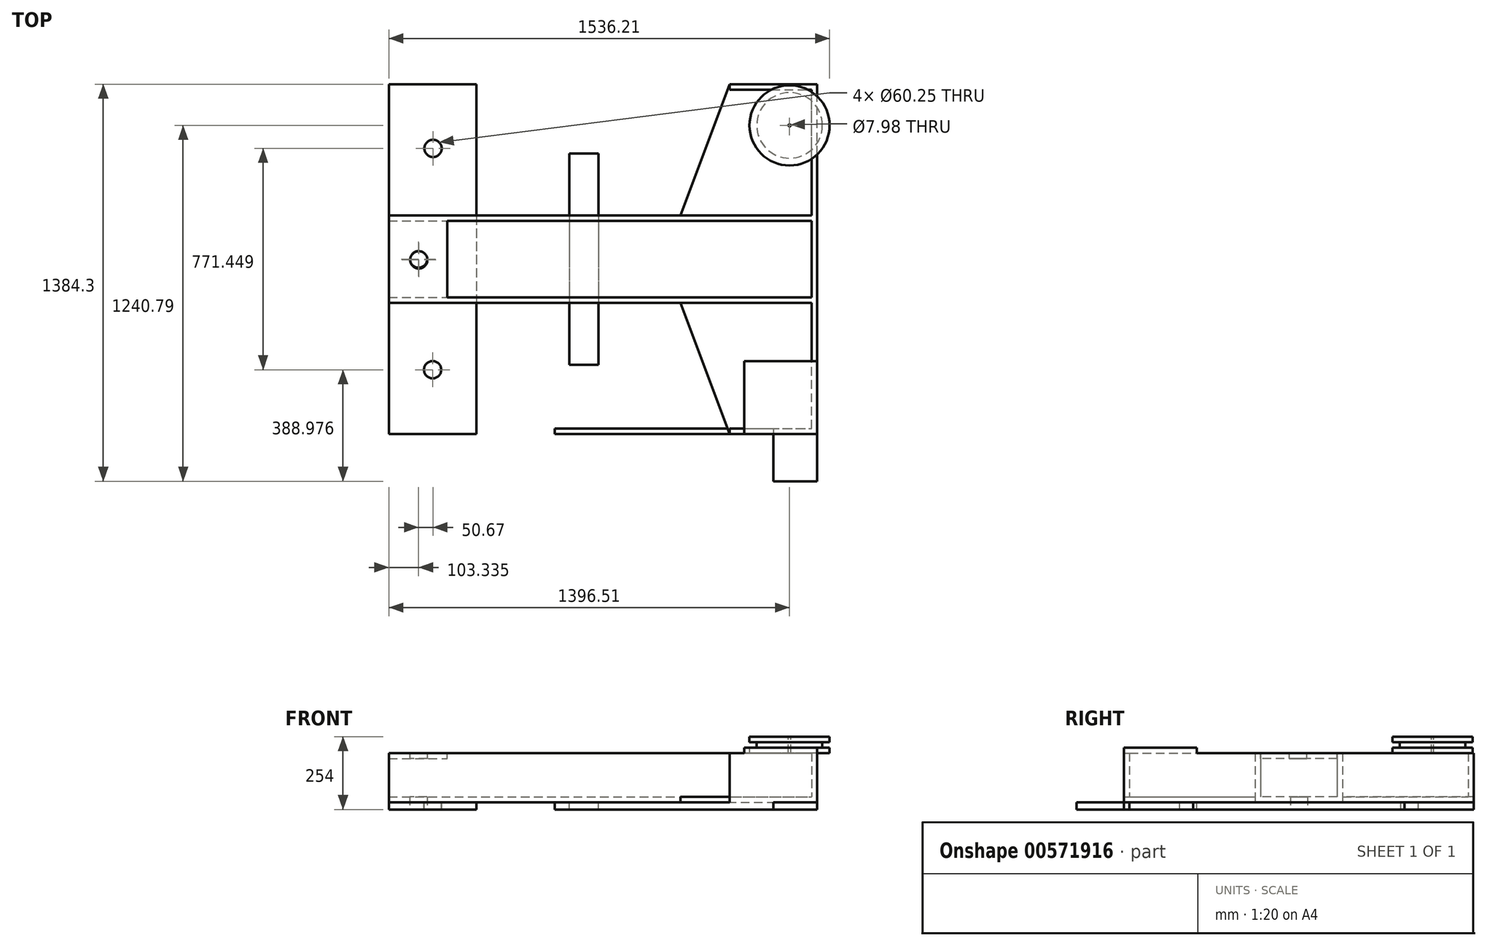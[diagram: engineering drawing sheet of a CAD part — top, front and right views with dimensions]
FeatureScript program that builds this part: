
annotation { "Feature Type Name" : "Feature", "Feature Type Description" : "" }
export const myFeature = defineFeature(function(context is Context, id is Id, definition is map)
    precondition{}
    {
        {
            var Q0;
            Q0=qCreatedBy(makeId("Top.planeOp"),FACE);
            var sketch = newSketch(context, id + "F0", { "sketchPlane" : qUnion([Q0])});
            skLineSegment(sketch, "E0.left", {"start": v(0, 0) * mm, "end": v(0, 1219.2) * mm});
            skLineSegment(sketch, "E1.bottom", {"start": v(-1492.4, 762) * mm, "end": v(-476.4, 762) * mm});
            skLineSegment(sketch, "E1.top", {"start": v(-1492.4, 457.2) * mm, "end": v(-476.4, 457.2) * mm});
            skLineSegment(sketch, "E1.left", {"start": v(-1492.4, 762) * mm, "end": v(-1492.4, 457.2) * mm});
            skLineSegment(sketch, "E1.right", {"start": v(-476.4, 762) * mm, "end": v(-476.4, 457.2) * mm});
            skPoint(sketch, "E2.oppositeSnap0", {"position": v(-1289.2, 914.4) * mm});
            skCircle(sketch, "E3", {"center": v(-1389.08, 609.6) * mm, "radius": 30.12 * mm});
            skPoint(sketch, "E3.centerSnap0", {"position": v(-1492.4, 609.6) * mm});
            skLineSegment(sketch, "E4.bottom", {"start": v(-1492.4, 457.2) * mm, "end": v(0, 457.2) * mm});
            skLineSegment(sketch, "E4.top", {"start": v(-1492.4, 476.25) * mm, "end": v(0, 476.25) * mm});
            skLineSegment(sketch, "E4.left", {"start": v(-1492.4, 457.2) * mm, "end": v(-1492.4, 476.25) * mm});
            skLineSegment(sketch, "E4.right", {"start": v(0, 457.2) * mm, "end": v(0, 476.25) * mm});
            skLineSegment(sketch, "E5.top", {"start": v(-1492.4, 742.95) * mm, "end": v(0, 742.95) * mm});
            skLineSegment(sketch, "E5.left", {"start": v(-1492.4, 762) * mm, "end": v(-1492.4, 742.95) * mm});
            skLineSegment(sketch, "E5.right", {"start": v(0, 762) * mm, "end": v(0, 742.95) * mm});
            skLineSegment(sketch, "E6", {"start": v(0, 0) * mm, "end": v(-304.8, 0) * mm});
            skLineSegment(sketch, "E7", {"start": v(-304.8, 0) * mm, "end": v(-476.4, 457.2) * mm});
            skLineSegment(sketch, "E8", {"start": v(0, 1219.2) * mm, "end": v(-304.8, 1219.2) * mm});
            skLineSegment(sketch, "E9", {"start": v(-304.8, 1219.2) * mm, "end": v(-476.4, 762) * mm});
            skSolve(sketch);
        }
        {
            var Q0;
            Q0 = qSketchRegion(id + "F0", true);
            extrude(context, id + "F1", {"entities" : qUnion([Q0]), "depth" : 19.05 * mm, "offsetDistance" : 25.4 * mm});
        }
        {
            var Q0;
            {var subQ0=sQuery(id+"F0.wireOp",EDGE,"E7");var subQ1=sQuery(id+"F0.wireOp",EDGE,"E6");var subQ2=sQuery(id+"F0.wireOp",EDGE,"E5.bottom");var subQ3=sQuery(id+"F0.wireOp",EDGE,"E8");var subQ4=sQuery(id+"F0.wireOp",EDGE,"E5.right");var subQ5=sQuery(id+"F0.wireOp",EDGE,"E4.right");var subQ6=sQuery(id+"F0.wireOp",EDGE,"E0.left");var subQ7=sQuery(id+"F0.wireOp",EDGE,"E9");var subQ8=sQuery(id+"F0.wireOp",EDGE,"E5.left");var subQ9=sQuery(id+"F0.wireOp",EDGE,"E4.left");var subQ10=sQuery(id+"F0.wireOp",EDGE,"E2.left");var subQ11=sQuery(id+"F0.wireOp",EDGE,"wJzC2NFF-3wZo-U59V-ZQ7f-zWFnnq6j3m8u.left");var subQ12=sQuery(id+"F0.wireOp",EDGE,"E1.left");var subQ13=sQuery(id+"F0.wireOp",EDGE,"E3");var subQ14=sQuery(id+"F0.wireOp",EDGE,"E4.bottom");Q0=makeQuery(id+"FyOnbS3y8ugpvit_1.boolean.opBoolean","SPLIT",FACE,{"disambiguationData":[TD([makeQuery(id+"F1.opExtrude","SWEPT_FACE",FACE,{"disambiguationData":[OSD([subQ13])]})])],"derivedFrom":makeQuery(id+"F1.opExtrude","CAP_FACE",FACE,{"disambiguationData":[OSD([subQ6,subQ12,sQuery(id+"F0.wireOp",EDGE,"wJzC2NFF-3wZo-U59V-ZQ7f-zWFnnq6j3m8u.top"),subQ11,sQuery(id+"F0.wireOp",EDGE,"wJzC2NFF-3wZo-U59V-ZQ7f-zWFnnq6j3m8u.right"),sQuery(id+"F0.wireOp",EDGE,"E2.top"),subQ10,sQuery(id+"F0.wireOp",EDGE,"E2.right"),subQ13,subQ14,subQ9,subQ5,subQ2,subQ8,subQ4,subQ1,subQ0,subQ3,subQ7])],"isStart":false})});}
            var sketch = newSketch(context, id + "F2", { "sketchPlane" : qUnion([Q0])});
            skLineSegment(sketch, "E10", {"start": v(0, 0) * mm, "end": v(-19.05, 0) * mm});
            skLineSegment(sketch, "E11", {"start": v(-19.05, 0) * mm, "end": v(-19.05, 1219.2) * mm});
            skLineSegment(sketch, "E12", {"start": v(-19.05, 1219.2) * mm, "end": v(0, 1219.2) * mm});
            skLineSegment(sketch, "E13", {"start": v(0, 1219.2) * mm, "end": v(0, 0) * mm});
            skSolve(sketch);
        }
        {
            var Q0;
            Q0=makeQuery(id+"F2.imprint","IMPRINT",FACE,{"disambiguationData":[TD([[makeQuery(id+"F2.imprint","IMPRINT",EDGE,{"derivedFrom":sQuery(id+"F2.wireOp",EDGE,"E10")}),-1.0]])]});
            extrude(context, id + "F3", {"entities" : qUnion([Q0]), "operationType" : NewBodyOperationType.ADD, "depth" : 152.4 * mm, "offsetDistance" : 25.4 * mm});
        }
        {
            var Q0;
            {var subQ0=sQuery(id+"F0.wireOp",EDGE,"E7");var subQ1=sQuery(id+"F0.wireOp",EDGE,"E6");var subQ2=sQuery(id+"F0.wireOp",EDGE,"E5.bottom");var subQ3=sQuery(id+"F0.wireOp",EDGE,"E8");var subQ4=sQuery(id+"F0.wireOp",EDGE,"E5.right");var subQ5=sQuery(id+"F0.wireOp",EDGE,"E4.right");var subQ6=sQuery(id+"F0.wireOp",EDGE,"E0.left");var subQ7=sQuery(id+"F0.wireOp",EDGE,"E9");var subQ8=sQuery(id+"F0.wireOp",EDGE,"E5.left");var subQ9=sQuery(id+"F0.wireOp",EDGE,"E4.left");var subQ10=sQuery(id+"F0.wireOp",EDGE,"E2.left");var subQ11=sQuery(id+"F0.wireOp",EDGE,"wJzC2NFF-3wZo-U59V-ZQ7f-zWFnnq6j3m8u.left");var subQ12=sQuery(id+"F0.wireOp",EDGE,"E1.left");var subQ13=sQuery(id+"F0.wireOp",EDGE,"E3");var subQ14=sQuery(id+"F0.wireOp",EDGE,"E4.bottom");Q0=makeQuery(id+"FyOnbS3y8ugpvit_1.boolean.opBoolean","SPLIT",FACE,{"disambiguationData":[TD([makeQuery(id+"F1.opExtrude","SWEPT_FACE",FACE,{"disambiguationData":[OSD([subQ13])]})])],"derivedFrom":makeQuery(id+"F1.opExtrude","CAP_FACE",FACE,{"disambiguationData":[OSD([subQ6,subQ12,sQuery(id+"F0.wireOp",EDGE,"wJzC2NFF-3wZo-U59V-ZQ7f-zWFnnq6j3m8u.top"),subQ11,sQuery(id+"F0.wireOp",EDGE,"wJzC2NFF-3wZo-U59V-ZQ7f-zWFnnq6j3m8u.right"),sQuery(id+"F0.wireOp",EDGE,"E2.top"),subQ10,sQuery(id+"F0.wireOp",EDGE,"E2.right"),subQ13,subQ14,subQ9,subQ5,subQ2,subQ8,subQ4,subQ1,subQ0,subQ3,subQ7])],"isStart":false})});}
            var sketch = newSketch(context, id + "F4", { "sketchPlane" : qUnion([Q0])});
            skLineSegment(sketch, "E14", {"start": v(-19.05, 0) * mm, "end": v(-304.8, 0) * mm});
            skLineSegment(sketch, "E15", {"start": v(-304.8, 0) * mm, "end": v(-304.8, 19.05) * mm});
            skLineSegment(sketch, "E16", {"start": v(-304.8, 19.05) * mm, "end": v(-19.05, 19.05) * mm});
            skLineSegment(sketch, "E17", {"start": v(-19.05, 19.05) * mm, "end": v(-19.05, 0) * mm});
            skLineSegment(sketch, "E18", {"start": v(-19.05, 1219.2) * mm, "end": v(-304.8, 1219.2) * mm});
            skLineSegment(sketch, "E19", {"start": v(-304.8, 1219.2) * mm, "end": v(-304.8, 1200.15) * mm});
            skLineSegment(sketch, "E20", {"start": v(-304.8, 1200.15) * mm, "end": v(-19.05, 1200.15) * mm});
            skLineSegment(sketch, "E21", {"start": v(-19.05, 1200.15) * mm, "end": v(-19.05, 1219.2) * mm});
            skSolve(sketch);
        }
        {
            var Q0;
            Q0=makeQuery(id+"F4.imprint","IMPRINT",FACE,{"disambiguationData":[TD([[makeQuery(id+"F4.imprint","IMPRINT",EDGE,{"derivedFrom":sQuery(id+"F4.wireOp",EDGE,"E14")}),-1.0]])]});
            var Q1;
            Q1=makeQuery(id+"F4.imprint","IMPRINT",FACE,{"disambiguationData":[TD([[makeQuery(id+"F4.imprint","IMPRINT",EDGE,{"derivedFrom":sQuery(id+"F4.wireOp",EDGE,"E18")}),1.0]])]});
            extrude(context, id + "F5", {"entities" : qUnion([Q0, Q1]), "operationType" : NewBodyOperationType.ADD, "depth" : 152.4 * mm, "offsetDistance" : 25.4 * mm});
        }
        {
            var Q0;
            Q0=makeQuery(id+"F1.opExtrude","CAP_FACE",FACE,{"disambiguationData":[OSD([sQuery(id+"F0.wireOp",EDGE,"E0.left"),sQuery(id+"F0.wireOp",EDGE,"E1.bottom"),sQuery(id+"F0.wireOp",EDGE,"E1.left"),sQuery(id+"F0.wireOp",EDGE,"E3"),sQuery(id+"F0.wireOp",EDGE,"E4.bottom"),sQuery(id+"F0.wireOp",EDGE,"E4.left"),sQuery(id+"F0.wireOp",EDGE,"E4.right"),sQuery(id+"F0.wireOp",EDGE,"E5.left"),sQuery(id+"F0.wireOp",EDGE,"E5.right"),sQuery(id+"F0.wireOp",EDGE,"E6"),sQuery(id+"F0.wireOp",EDGE,"E7"),sQuery(id+"F0.wireOp",EDGE,"E8"),sQuery(id+"F0.wireOp",EDGE,"E9")])],"isStart":false});
            var sketch = newSketch(context, id + "F6", { "sketchPlane" : qUnion([Q0])});
            skLineSegment(sketch, "E22.bottom", {"start": v(-1492.4, 762) * mm, "end": v(-19.05, 762) * mm});
            skLineSegment(sketch, "E22.top", {"start": v(-1492.4, 742.95) * mm, "end": v(-19.05, 742.95) * mm});
            skLineSegment(sketch, "E22.left", {"start": v(-1492.4, 762) * mm, "end": v(-1492.4, 742.95) * mm});
            skLineSegment(sketch, "E22.right", {"start": v(-19.05, 762) * mm, "end": v(-19.05, 742.95) * mm});
            skLineSegment(sketch, "E23.bottom", {"start": v(-1492.4, 457.2) * mm, "end": v(-19.05, 457.2) * mm});
            skLineSegment(sketch, "E23.top", {"start": v(-1492.4, 476.25) * mm, "end": v(-19.05, 476.25) * mm});
            skLineSegment(sketch, "E23.left", {"start": v(-1492.4, 457.2) * mm, "end": v(-1492.4, 476.25) * mm});
            skLineSegment(sketch, "E23.right", {"start": v(-19.05, 457.2) * mm, "end": v(-19.05, 476.25) * mm});
            skSolve(sketch);
        }
        {
            var Q0;
            Q0=makeQuery(id+"F6.imprint","IMPRINT",FACE,{"disambiguationData":[TD([[makeQuery(id+"F6.imprint","IMPRINT",EDGE,{"derivedFrom":sQuery(id+"F6.wireOp",EDGE,"E22.top")}),1.0]])]});
            var Q1;
            Q1=makeQuery(id+"F6.imprint","IMPRINT",FACE,{"disambiguationData":[TD([[makeQuery(id+"F6.imprint","IMPRINT",EDGE,{"derivedFrom":sQuery(id+"F6.wireOp",EDGE,"E23.top")}),-1.0]])]});
            extrude(context, id + "F7", {"entities" : qUnion([Q0, Q1]), "operationType" : NewBodyOperationType.ADD, "depth" : 152.4 * mm, "offsetDistance" : 25.4 * mm});
        }
        {
            var Q0;
            Q0=makeQuery(id+"F7.boolean.opBoolean","MERGE",FACE,{"derivedFrom":[makeQuery(id+"F5.boolean.opBoolean","MERGE",FACE,{"derivedFrom":[makeQuery(id+"F3.opExtrude","CAP_FACE",FACE,{"disambiguationData":[OSD([sQuery(id+"F2.wireOp",EDGE,"E10"),sQuery(id+"F2.wireOp",EDGE,"E11"),sQuery(id+"F2.wireOp",EDGE,"E12"),sQuery(id+"F2.wireOp",EDGE,"E13")])],"isStart":false}),makeQuery(id+"F5.opExtrude","CAP_FACE",FACE,{"disambiguationData":[OSD([sQuery(id+"F4.wireOp",EDGE,"E14"),sQuery(id+"F4.wireOp",EDGE,"E15"),sQuery(id+"F4.wireOp",EDGE,"E16"),sQuery(id+"F4.wireOp",EDGE,"E17")])],"isStart":false}),makeQuery(id+"F5.opExtrude","CAP_FACE",FACE,{"disambiguationData":[OSD([sQuery(id+"F4.wireOp",EDGE,"E18"),sQuery(id+"F4.wireOp",EDGE,"E19"),sQuery(id+"F4.wireOp",EDGE,"E20"),sQuery(id+"F4.wireOp",EDGE,"E21")])],"isStart":false})]}),makeQuery(id+"F7.opExtrude","CAP_FACE",FACE,{"disambiguationData":[OSD([sQuery(id+"F6.wireOp",EDGE,"E22.bottom"),sQuery(id+"F6.wireOp",EDGE,"E22.top"),sQuery(id+"F6.wireOp",EDGE,"E22.left"),sQuery(id+"F6.wireOp",EDGE,"E22.right")])],"isStart":false}),makeQuery(id+"F7.opExtrude","CAP_FACE",FACE,{"disambiguationData":[OSD([sQuery(id+"F6.wireOp",EDGE,"E23.bottom"),sQuery(id+"F6.wireOp",EDGE,"E23.top"),sQuery(id+"F6.wireOp",EDGE,"E23.left"),sQuery(id+"F6.wireOp",EDGE,"E23.right")])],"isStart":false})]});
            var sketch = newSketch(context, id + "F8", { "sketchPlane" : qUnion([Q0])});
            skLineSegment(sketch, "E24", {"start": v(-1492.4, 742.95) * mm, "end": v(-1492.4, 476.25) * mm});
            skLineSegment(sketch, "E25", {"start": v(-1492.4, 476.25) * mm, "end": v(-1289.2, 476.25) * mm});
            skLineSegment(sketch, "E26", {"start": v(-1289.2, 476.25) * mm, "end": v(-1289.2, 742.95) * mm});
            skLineSegment(sketch, "E27", {"start": v(-1289.2, 742.95) * mm, "end": v(-1492.4, 742.95) * mm});
            skCircle(sketch, "E28", {"center": v(-1388.19, 606.77) * mm, "radius": 30.12 * mm});
            skLineSegment(sketch, "E29.0.0", {"start": v(-19.05, 457.2) * mm, "end": v(-19.05, 19.05) * mm});
            skLineSegment(sketch, "E29.0.1", {"start": v(-19.05, 19.05) * mm, "end": v(-304.8, 19.05) * mm});
            skLineSegment(sketch, "E29.0.2", {"start": v(-304.8, 19.05) * mm, "end": v(-304.8, 0) * mm});
            skLineSegment(sketch, "E29.0.3", {"start": v(-304.8, 0) * mm, "end": v(0, 0) * mm});
            skLineSegment(sketch, "E29.0.4", {"start": v(0, 0) * mm, "end": v(0, 1219.2) * mm});
            skLineSegment(sketch, "E29.0.5", {"start": v(0, 1219.2) * mm, "end": v(-304.8, 1219.2) * mm});
            skLineSegment(sketch, "E29.0.6", {"start": v(-304.8, 1219.2) * mm, "end": v(-304.8, 1200.15) * mm});
            skLineSegment(sketch, "E29.0.7", {"start": v(-304.8, 1200.15) * mm, "end": v(-19.05, 1200.15) * mm});
            skLineSegment(sketch, "E29.0.8", {"start": v(-19.05, 1200.15) * mm, "end": v(-19.05, 762) * mm});
            skLineSegment(sketch, "E29.0.9", {"start": v(-19.05, 762) * mm, "end": v(-1492.4, 762) * mm});
            skLineSegment(sketch, "E29.0.10", {"start": v(-1492.4, 762) * mm, "end": v(-1492.4, 742.95) * mm});
            skLineSegment(sketch, "E29.0.11", {"start": v(-1492.4, 742.95) * mm, "end": v(-19.05, 742.95) * mm});
            skLineSegment(sketch, "E29.0.12", {"start": v(-19.05, 742.95) * mm, "end": v(-19.05, 476.25) * mm});
            skLineSegment(sketch, "E29.0.13", {"start": v(-19.05, 476.25) * mm, "end": v(-1492.4, 476.25) * mm});
            skLineSegment(sketch, "E29.0.14", {"start": v(-1492.4, 476.25) * mm, "end": v(-1492.4, 457.2) * mm});
            skLineSegment(sketch, "E29.0.15", {"start": v(-1492.4, 457.2) * mm, "end": v(-19.05, 457.2) * mm});
            skSolve(sketch);
        }
        {
            var Q0;
            Q0 = qSketchRegion(id + "F8", true);
            extrude(context, id + "F9", {"entities" : qUnion([Q0]), "operationType" : NewBodyOperationType.ADD, "oppositeDirection" : true, "depth" : 19.05 * mm, "offsetDistance" : 25.4 * mm});
        }
        {
            var Q0;
            Q0=makeQuery(id+"F9.boolean.opBoolean","MERGE",FACE,{"derivedFrom":[makeQuery(id+"F7.boolean.opBoolean","MERGE",FACE,{"derivedFrom":[makeQuery(id+"F5.boolean.opBoolean","MERGE",FACE,{"derivedFrom":[makeQuery(id+"F3.opExtrude","CAP_FACE",FACE,{"disambiguationData":[OSD([sQuery(id+"F2.wireOp",EDGE,"E10"),sQuery(id+"F2.wireOp",EDGE,"E11"),sQuery(id+"F2.wireOp",EDGE,"E12"),sQuery(id+"F2.wireOp",EDGE,"E13")])],"isStart":false}),makeQuery(id+"F5.opExtrude","CAP_FACE",FACE,{"disambiguationData":[OSD([sQuery(id+"F4.wireOp",EDGE,"E14"),sQuery(id+"F4.wireOp",EDGE,"E15"),sQuery(id+"F4.wireOp",EDGE,"E16"),sQuery(id+"F4.wireOp",EDGE,"E17")])],"isStart":false}),makeQuery(id+"F5.opExtrude","CAP_FACE",FACE,{"disambiguationData":[OSD([sQuery(id+"F4.wireOp",EDGE,"E18"),sQuery(id+"F4.wireOp",EDGE,"E19"),sQuery(id+"F4.wireOp",EDGE,"E20"),sQuery(id+"F4.wireOp",EDGE,"E21")])],"isStart":false})]}),makeQuery(id+"F7.opExtrude","CAP_FACE",FACE,{"disambiguationData":[OSD([sQuery(id+"F6.wireOp",EDGE,"E22.bottom"),sQuery(id+"F6.wireOp",EDGE,"E22.top"),sQuery(id+"F6.wireOp",EDGE,"E22.left"),sQuery(id+"F6.wireOp",EDGE,"E22.right")])],"isStart":false}),makeQuery(id+"F7.opExtrude","CAP_FACE",FACE,{"disambiguationData":[OSD([sQuery(id+"F6.wireOp",EDGE,"E23.bottom"),sQuery(id+"F6.wireOp",EDGE,"E23.top"),sQuery(id+"F6.wireOp",EDGE,"E23.left"),sQuery(id+"F6.wireOp",EDGE,"E23.right")])],"isStart":false})]}),makeQuery(id+"F9.opExtrude","CAP_FACE",FACE,{"disambiguationData":[OSD([sQuery(id+"F8.wireOp",EDGE,"E24"),sQuery(id+"F8.wireOp",EDGE,"E25"),sQuery(id+"F8.wireOp",EDGE,"E26"),sQuery(id+"F8.wireOp",EDGE,"E27"),sQuery(id+"F8.wireOp",EDGE,"E28")])],"isStart":true})]});
            var sketch = newSketch(context, id + "F10", { "sketchPlane" : qUnion([Q0])});
            skLineSegment(sketch, "E30", {"start": v(-19.05, 1019.81) * mm, "end": v(-199.4, 1200.15) * mm});
            skLineSegment(sketch, "E31", {"start": v(-199.4, 1200.15) * mm, "end": v(-237.5, 1200.15) * mm});
            skLineSegment(sketch, "E32", {"start": v(-19.05, 1019.81) * mm, "end": v(-19.05, 981.71) * mm});
            skLineSegment(sketch, "E33", {"start": v(-19.05, 981.71) * mm, "end": v(-237.49, 1200.15) * mm});
            skLineSegment(sketch, "E34", {"start": v(-19.05, 19.05) * mm, "end": v(-199.92, 19.05) * mm});
            skSolve(sketch);
        }
        {
            var Q0;
            Q0 = qSketchRegion(id + "F10", true);
            extrude(context, id + "F11", {"entities" : qUnion([Q0]), "oppositeDirection" : true, "depth" : 19.05 * mm, "offsetDistance" : 25.4 * mm});
        }
        {
            var Q0;
            Q0=makeQuery(id+"F11.boolean.opBoolean","MERGE",FACE,{"derivedFrom":[makeQuery(id+"F9.boolean.opBoolean","MERGE",FACE,{"derivedFrom":[makeQuery(id+"F7.boolean.opBoolean","MERGE",FACE,{"derivedFrom":[makeQuery(id+"F5.boolean.opBoolean","MERGE",FACE,{"derivedFrom":[makeQuery(id+"F3.opExtrude","CAP_FACE",FACE,{"disambiguationData":[OSD([sQuery(id+"F2.wireOp",EDGE,"E10"),sQuery(id+"F2.wireOp",EDGE,"E11"),sQuery(id+"F2.wireOp",EDGE,"E12"),sQuery(id+"F2.wireOp",EDGE,"E13")])],"isStart":false}),makeQuery(id+"F5.opExtrude","CAP_FACE",FACE,{"disambiguationData":[OSD([sQuery(id+"F4.wireOp",EDGE,"E14"),sQuery(id+"F4.wireOp",EDGE,"E15"),sQuery(id+"F4.wireOp",EDGE,"E16"),sQuery(id+"F4.wireOp",EDGE,"E17")])],"isStart":false}),makeQuery(id+"F5.opExtrude","CAP_FACE",FACE,{"disambiguationData":[OSD([sQuery(id+"F4.wireOp",EDGE,"E18"),sQuery(id+"F4.wireOp",EDGE,"E19"),sQuery(id+"F4.wireOp",EDGE,"E20"),sQuery(id+"F4.wireOp",EDGE,"E21")])],"isStart":false})]}),makeQuery(id+"F7.opExtrude","CAP_FACE",FACE,{"disambiguationData":[OSD([sQuery(id+"F6.wireOp",EDGE,"E22.bottom"),sQuery(id+"F6.wireOp",EDGE,"E22.top"),sQuery(id+"F6.wireOp",EDGE,"E22.left"),sQuery(id+"F6.wireOp",EDGE,"E22.right")])],"isStart":false}),makeQuery(id+"F7.opExtrude","CAP_FACE",FACE,{"disambiguationData":[OSD([sQuery(id+"F6.wireOp",EDGE,"E23.bottom"),sQuery(id+"F6.wireOp",EDGE,"E23.top"),sQuery(id+"F6.wireOp",EDGE,"E23.left"),sQuery(id+"F6.wireOp",EDGE,"E23.right")])],"isStart":false})]}),makeQuery(id+"F9.opExtrude","CAP_FACE",FACE,{"disambiguationData":[OSD([sQuery(id+"F8.wireOp",EDGE,"E24"),sQuery(id+"F8.wireOp",EDGE,"E25"),sQuery(id+"F8.wireOp",EDGE,"E26"),sQuery(id+"F8.wireOp",EDGE,"E27"),sQuery(id+"F8.wireOp",EDGE,"E28")])],"isStart":true})]}),makeQuery(id+"F11.opExtrude","CAP_FACE",FACE,{"disambiguationData":[OSD([sQuery(id+"F10.wireOp",EDGE,"etS2MnEX-B9NU-Zd02-58En-28LzD7IUnOs5"),sQuery(id+"F10.wireOp",EDGE,"MPMmyaxD-GanR-Jw2c-mU0s-mxgsOwT9cw53"),sQuery(id+"F10.wireOp",EDGE,"5WOe5Nc3-rlZ5-iHml-zvMP-gz4QLQMEJuns"),sQuery(id+"F10.wireOp",EDGE,"06NhnlFu-nvfy-ftOh-3kmv-3FOc10eu5HYR")])],"isStart":true})]});
            var sketch = newSketch(context, id + "F12", { "sketchPlane" : qUnion([Q0])});
            skCircle(sketch, "E35", {"center": v(-95.9, 1075.69) * mm, "radius": 139.7 * mm});
            skSolve(sketch);
        }
        {
            var Q0;
            Q0 = qSketchRegion(id + "F12", true);
            extrude(context, id + "F13", {"entities" : qUnion([Q0]), "operationType" : NewBodyOperationType.ADD, "depth" : 19.05 * mm, "offsetDistance" : 25.4 * mm});
        }
        {
            var Q0;
            Q0=makeQuery(id+"F13.opExtrude","CAP_FACE",FACE,{"disambiguationData":[OSD([sQuery(id+"F12.wireOp",EDGE,"E35")])],"isStart":false});
            var sketch = newSketch(context, id + "F14", { "sketchPlane" : qUnion([Q0])});
            skCircle(sketch, "E36", {"center": v(-95.9, 1075.69) * mm, "radius": 114.3 * mm});
            skSolve(sketch);
        }
        {
            var Q0;
            Q0 = qSketchRegion(id + "F14", true);
            extrude(context, id + "F15", {"entities" : qUnion([Q0]), "operationType" : NewBodyOperationType.ADD, "depth" : 19.05 * mm, "offsetDistance" : 25.4 * mm});
        }
        {
            var Q0;
            Q0=makeQuery(id+"F15.opExtrude","CAP_FACE",FACE,{"disambiguationData":[OSD([sQuery(id+"F14.wireOp",EDGE,"E36")])],"isStart":false});
            var sketch = newSketch(context, id + "F16", { "sketchPlane" : qUnion([Q0])});
            skCircle(sketch, "E37", {"center": v(-95.9, 1075.69) * mm, "radius": 139.7 * mm});
            skSolve(sketch);
        }
        {
            var Q0;
            Q0 = qSketchRegion(id + "F16", true);
            extrude(context, id + "F17", {"entities" : qUnion([Q0]), "operationType" : NewBodyOperationType.ADD, "depth" : 19.05 * mm, "offsetDistance" : 25.4 * mm});
        }
        {
            var Q0;
            Q0=makeQuery(id+"F1.opExtrude","CAP_FACE",FACE,{"disambiguationData":[OSD([sQuery(id+"F0.wireOp",EDGE,"E0.left"),sQuery(id+"F0.wireOp",EDGE,"E1.bottom"),sQuery(id+"F0.wireOp",EDGE,"E1.left"),sQuery(id+"F0.wireOp",EDGE,"E3"),sQuery(id+"F0.wireOp",EDGE,"E4.bottom"),sQuery(id+"F0.wireOp",EDGE,"E4.left"),sQuery(id+"F0.wireOp",EDGE,"E4.right"),sQuery(id+"F0.wireOp",EDGE,"E5.left"),sQuery(id+"F0.wireOp",EDGE,"E5.right"),sQuery(id+"F0.wireOp",EDGE,"E6"),sQuery(id+"F0.wireOp",EDGE,"E7"),sQuery(id+"F0.wireOp",EDGE,"E8"),sQuery(id+"F0.wireOp",EDGE,"E9")])],"isStart":true});
            var sketch = newSketch(context, id + "F18", { "sketchPlane" : qUnion([Q0])});
            skLineSegment(sketch, "E38.bottom", {"start": v(-863.6, -977.9) * mm, "end": v(-762, -977.9) * mm});
            skLineSegment(sketch, "E38.top", {"start": v(-863.6, -241.3) * mm, "end": v(-762, -241.3) * mm});
            skLineSegment(sketch, "E38.left", {"start": v(-863.6, -977.9) * mm, "end": v(-863.6, -241.3) * mm});
            skLineSegment(sketch, "E38.right", {"start": v(-762, -977.9) * mm, "end": v(-762, -241.3) * mm});
            skSolve(sketch);
        }
        {
            var Q0;
            Q0 = qSketchRegion(id + "F10", true);
            extrude(context, id + "F19", {"entities" : qUnion([Q0]), "operationType" : NewBodyOperationType.REMOVE, "oppositeDirection" : true, "depth" : 19.05 * mm, "offsetDistance" : 25.4 * mm});
        }
        {
            var Q0;
            Q0 = qSketchRegion(id + "F18", true);
            extrude(context, id + "F20", {"entities" : qUnion([Q0]), "operationType" : NewBodyOperationType.ADD, "depth" : 25.4 * mm, "offsetDistance" : 25.4 * mm});
        }
        {
            var Q0;
            Q0=makeQuery(id+"F17.opExtrude","CAP_FACE",FACE,{"disambiguationData":[OSD([sQuery(id+"F16.wireOp",EDGE,"E37")])],"isStart":false});
            var sketch = newSketch(context, id + "F21", { "sketchPlane" : qUnion([Q0])});
            skCircle(sketch, "E39", {"center": v(-95.9, 1075.69) * mm, "radius": 3.99 * mm});
            skSolve(sketch);
        }
        {
            var Q0;
            Q0 = qSketchRegion(id + "F21", true);
            extrude(context, id + "F22", {"entities" : qUnion([Q0]), "operationType" : NewBodyOperationType.REMOVE, "oppositeDirection" : true, "depth" : 96.52 * mm, "offsetDistance" : 25.4 * mm});
        }
        {
            var Q0;
            {var subQ0=sQuery(id+"F0.wireOp",EDGE,"E1.bottom");var subQ1=sQuery(id+"F0.wireOp",EDGE,"E5.left");var subQ2=sQuery(id+"F0.wireOp",EDGE,"E4.left");var subQ3=sQuery(id+"F0.wireOp",EDGE,"E1.left");var subQ4=sQuery(id+"F0.wireOp",EDGE,"E3");var subQ6=sQuery(id+"F0.wireOp",EDGE,"E4.bottom");Q0=makeQuery(id+"F20.boolean.opBoolean","SPLIT",FACE,{"disambiguationData":[TD([makeQuery(id+"F1.opExtrude","SWEPT_FACE",FACE,{"disambiguationData":[OSD([subQ4])]})])],"derivedFrom":makeQuery(id+"F1.opExtrude","CAP_FACE",FACE,{"disambiguationData":[OSD([sQuery(id+"F0.wireOp",EDGE,"E0.left"),subQ0,subQ3,subQ4,subQ6,subQ2,sQuery(id+"F0.wireOp",EDGE,"E4.right"),subQ1,sQuery(id+"F0.wireOp",EDGE,"E5.right"),sQuery(id+"F0.wireOp",EDGE,"E6"),sQuery(id+"F0.wireOp",EDGE,"E7"),sQuery(id+"F0.wireOp",EDGE,"E8"),sQuery(id+"F0.wireOp",EDGE,"E9")])],"isStart":true})});}
            var sketch = newSketch(context, id + "F23", { "sketchPlane" : qUnion([Q0])});
            skLineSegment(sketch, "E40.bottom", {"start": v(-1492.4, -1219.2) * mm, "end": v(-1187.6, -1219.2) * mm});
            skLineSegment(sketch, "E40.top", {"start": v(-1492.4, 0) * mm, "end": v(-1187.6, 0) * mm});
            skLineSegment(sketch, "E40.left", {"start": v(-1492.4, -1219.2) * mm, "end": v(-1492.4, 0) * mm});
            skLineSegment(sketch, "E40.right", {"start": v(-1187.6, -1219.2) * mm, "end": v(-1187.6, 0) * mm});
            skCircle(sketch, "E41", {"center": v(-1389.08, -609.6) * mm, "radius": 30.12 * mm});
            skCircle(sketch, "E42", {"center": v(-1338.4, -995.32) * mm, "radius": 30.12 * mm});
            skCircle(sketch, "E43", {"center": v(-1340, -223.88) * mm, "radius": 30.12 * mm});
            skLineSegment(sketch, "E44.0.0", {"start": v(-1492.4, -457.2) * mm, "end": v(-863.6, -457.2) * mm});
            skLineSegment(sketch, "E44.0.1", {"start": v(-863.6, -457.2) * mm, "end": v(-762, -457.2) * mm});
            skLineSegment(sketch, "E44.0.2", {"start": v(-762, -457.2) * mm, "end": v(-476.4, -457.2) * mm});
            skLineSegment(sketch, "E44.0.4", {"start": v(-476.4, -457.2) * mm, "end": v(-19.05, -457.2) * mm});
            skLineSegment(sketch, "E44.0.6", {"start": v(-19.05, -457.2) * mm, "end": v(-1492.4, -457.2) * mm});
            skLineSegment(sketch, "E45.0.0", {"start": v(-863.6, -762) * mm, "end": v(-1492.4, -762) * mm});
            skLineSegment(sketch, "E45.0.2", {"start": v(-1492.4, -762) * mm, "end": v(-19.05, -762) * mm});
            skLineSegment(sketch, "E45.0.4", {"start": v(-19.05, -762) * mm, "end": v(-476.4, -762) * mm});
            skLineSegment(sketch, "E45.0.6", {"start": v(-476.4, -762) * mm, "end": v(-762, -762) * mm});
            skLineSegment(sketch, "E45.0.7", {"start": v(-762, -762) * mm, "end": v(-863.6, -762) * mm});
            skSolve(sketch);
        }
        {
            var Q0;
            Q0 = qSketchRegion(id + "F23", true);
            extrude(context, id + "F24", {"entities" : qUnion([Q0]), "operationType" : NewBodyOperationType.ADD, "depth" : 25.4 * mm, "offsetDistance" : 25.4 * mm});
        }
        {
            var Q0;
            {var subQ0=sQuery(id+"F4.wireOp",EDGE,"E15");var subQ1=sQuery(id+"F8.wireOp",EDGE,"E24");var subQ2=sQuery(id+"F2.wireOp",EDGE,"E10");var subQ3=sQuery(id+"F2.wireOp",EDGE,"E11");var subQ4=sQuery(id+"F6.wireOp",EDGE,"E22.bottom");var subQ5=sQuery(id+"F8.wireOp",EDGE,"E28");var subQ6=sQuery(id+"F4.wireOp",EDGE,"E14");var subQ7=sQuery(id+"F6.wireOp",EDGE,"E23.left");var subQ8=sQuery(id+"F2.wireOp",EDGE,"E13");var subQ9=sQuery(id+"F4.wireOp",EDGE,"E16");var subQ10=sQuery(id+"F6.wireOp",EDGE,"E22.top");var subQ11=sQuery(id+"F6.wireOp",EDGE,"E22.left");var subQ12=sQuery(id+"F6.wireOp",EDGE,"E23.bottom");var subQ13=sQuery(id+"F6.wireOp",EDGE,"E23.top");var subQ14=sQuery(id+"F8.wireOp",EDGE,"E26");Q0=makeQuery(id+"F13.boolean.opBoolean","SPLIT",FACE,{"disambiguationData":[TD([makeQuery(id+"F1.opExtrude","SWEPT_FACE",FACE,{"disambiguationData":[OSD([sQuery(id+"F0.wireOp",EDGE,"E1.bottom")])]})])],"derivedFrom":makeQuery(id+"F9.boolean.opBoolean","MERGE",FACE,{"derivedFrom":[makeQuery(id+"F7.boolean.opBoolean","MERGE",FACE,{"derivedFrom":[makeQuery(id+"F5.boolean.opBoolean","MERGE",FACE,{"derivedFrom":[makeQuery(id+"F3.opExtrude","CAP_FACE",FACE,{"disambiguationData":[OSD([subQ2,subQ3,sQuery(id+"F2.wireOp",EDGE,"E12"),subQ8])],"isStart":false}),makeQuery(id+"F5.opExtrude","CAP_FACE",FACE,{"disambiguationData":[OSD([subQ6,subQ0,subQ9,sQuery(id+"F4.wireOp",EDGE,"E17")])],"isStart":false}),makeQuery(id+"F5.opExtrude","CAP_FACE",FACE,{"disambiguationData":[OSD([sQuery(id+"F4.wireOp",EDGE,"E18"),sQuery(id+"F4.wireOp",EDGE,"E19"),sQuery(id+"F4.wireOp",EDGE,"E20"),sQuery(id+"F4.wireOp",EDGE,"E21")])],"isStart":false})]}),makeQuery(id+"F7.opExtrude","CAP_FACE",FACE,{"disambiguationData":[OSD([subQ4,subQ10,subQ11,sQuery(id+"F6.wireOp",EDGE,"E22.right")])],"isStart":false}),makeQuery(id+"F7.opExtrude","CAP_FACE",FACE,{"disambiguationData":[OSD([subQ12,subQ13,subQ7,sQuery(id+"F6.wireOp",EDGE,"E23.right")])],"isStart":false})]}),makeQuery(id+"F9.opExtrude","CAP_FACE",FACE,{"disambiguationData":[OSD([subQ1,sQuery(id+"F8.wireOp",EDGE,"E25"),subQ14,sQuery(id+"F8.wireOp",EDGE,"E27"),subQ5])],"isStart":true})]})});}
            var sketch = newSketch(context, id + "F25", { "sketchPlane" : qUnion([Q0])});
            skLineSegment(sketch, "E46.bottom", {"start": v(0, 0) * mm, "end": v(-254, 0) * mm});
            skLineSegment(sketch, "E46.top", {"start": v(0, 254) * mm, "end": v(-254, 254) * mm});
            skLineSegment(sketch, "E46.left", {"start": v(0, 0) * mm, "end": v(0, 254) * mm});
            skLineSegment(sketch, "E46.right", {"start": v(-254, 0) * mm, "end": v(-254, 254) * mm});
            skSolve(sketch);
        }
        {
            var Q0;
            Q0 = qSketchRegion(id + "F25", true);
            extrude(context, id + "F26", {"entities" : qUnion([Q0]), "operationType" : NewBodyOperationType.ADD, "depth" : 19.05 * mm, "offsetDistance" : 25.4 * mm});
        }
        {
            var Q0;
            {var subQ0=sQuery(id+"F0.wireOp",EDGE,"E7");var subQ1=sQuery(id+"F0.wireOp",EDGE,"E9");var subQ2=sQuery(id+"F0.wireOp",EDGE,"E8");var subQ3=sQuery(id+"F0.wireOp",EDGE,"E5.right");var subQ4=sQuery(id+"F0.wireOp",EDGE,"E4.right");var subQ5=sQuery(id+"F0.wireOp",EDGE,"E0.left");var subQ6=sQuery(id+"F0.wireOp",EDGE,"E6");var subQ8=sQuery(id+"F0.wireOp",EDGE,"E1.bottom");var subQ9=sQuery(id+"F0.wireOp",EDGE,"E4.bottom");Q0=makeQuery(id+"F20.boolean.opBoolean","SPLIT",FACE,{"disambiguationData":[TD([makeQuery(id+"F1.opExtrude","SWEPT_FACE",FACE,{"disambiguationData":[OSD([subQ6])]})])],"derivedFrom":makeQuery(id+"F1.opExtrude","CAP_FACE",FACE,{"disambiguationData":[OSD([subQ5,subQ8,sQuery(id+"F0.wireOp",EDGE,"E1.left"),sQuery(id+"F0.wireOp",EDGE,"E3"),subQ9,sQuery(id+"F0.wireOp",EDGE,"E4.left"),subQ4,sQuery(id+"F0.wireOp",EDGE,"E5.left"),subQ3,subQ6,subQ0,subQ2,subQ1])],"isStart":true})});}
            var sketch = newSketch(context, id + "F27", { "sketchPlane" : qUnion([Q0])});
            skLineSegment(sketch, "E47.0.2", {"start": v(-304.8, 0) * mm, "end": v(0, 0) * mm});
            skLineSegment(sketch, "E48", {"start": v(-152.4, 0) * mm, "end": v(-914.4, 0) * mm});
            skLineSegment(sketch, "E49", {"start": v(-914.4, 0) * mm, "end": v(-914.4, -19.05) * mm});
            skLineSegment(sketch, "E50", {"start": v(-914.4, -19.05) * mm, "end": v(-152.4, -19.05) * mm});
            skLineSegment(sketch, "E51", {"start": v(-152.4, -19.05) * mm, "end": v(-152.4, 0) * mm});
            skSolve(sketch);
        }
        {
            var Q0;
            Q0 = qSketchRegion(id + "F27", true);
            extrude(context, id + "F28", {"entities" : qUnion([Q0]), "operationType" : NewBodyOperationType.ADD, "depth" : 25.4 * mm, "offsetDistance" : 25.4 * mm});
        }
        {
            var Q0;
            Q0=makeQuery(id+"F28.boolean.opBoolean","MERGE",FACE,{"derivedFrom":[makeQuery(id+"F26.boolean.opBoolean","MERGE",FACE,{"derivedFrom":[makeQuery(id+"F5.boolean.opBoolean","MERGE",FACE,{"derivedFrom":[makeQuery(id+"F3.boolean.opBoolean","MERGE",FACE,{"derivedFrom":[makeQuery(id+"F1.opExtrude","SWEPT_FACE",FACE,{"disambiguationData":[OSD([sQuery(id+"F0.wireOp",EDGE,"E6")])]}),makeQuery(id+"F3.opExtrude","SWEPT_FACE",FACE,{"disambiguationData":[OSD([sQuery(id+"F2.wireOp",EDGE,"E10")])]})]}),makeQuery(id+"F5.opExtrude","SWEPT_FACE",FACE,{"disambiguationData":[OSD([sQuery(id+"F4.wireOp",EDGE,"E14")])]})]}),makeQuery(id+"F26.opExtrude","SWEPT_FACE",FACE,{"disambiguationData":[OSD([sQuery(id+"F25.wireOp",EDGE,"E46.bottom")])]})]}),makeQuery(id+"F28.opExtrude","SWEPT_FACE",FACE,{"disambiguationData":[OSD([sQuery(id+"F27.wireOp",EDGE,"E48")])]})]});
            var sketch = newSketch(context, id + "F29", { "sketchPlane" : qUnion([Q0])});
            skLineSegment(sketch, "E52.bottom", {"start": v(-152.4, -25.4) * mm, "end": v(0, -25.4) * mm});
            skLineSegment(sketch, "E52.top", {"start": v(-152.4, 0) * mm, "end": v(0, 0) * mm});
            skLineSegment(sketch, "E52.left", {"start": v(-152.4, -25.4) * mm, "end": v(-152.4, 0) * mm});
            skLineSegment(sketch, "E52.right", {"start": v(0, -25.4) * mm, "end": v(0, 0) * mm});
            skSolve(sketch);
        }
        {
            var Q0;
            Q0 = qSketchRegion(id + "F29", true);
            extrude(context, id + "F30", {"entities" : qUnion([Q0]), "depth" : 165.1 * mm, "offsetDistance" : 25.4 * mm});
        }
    });
